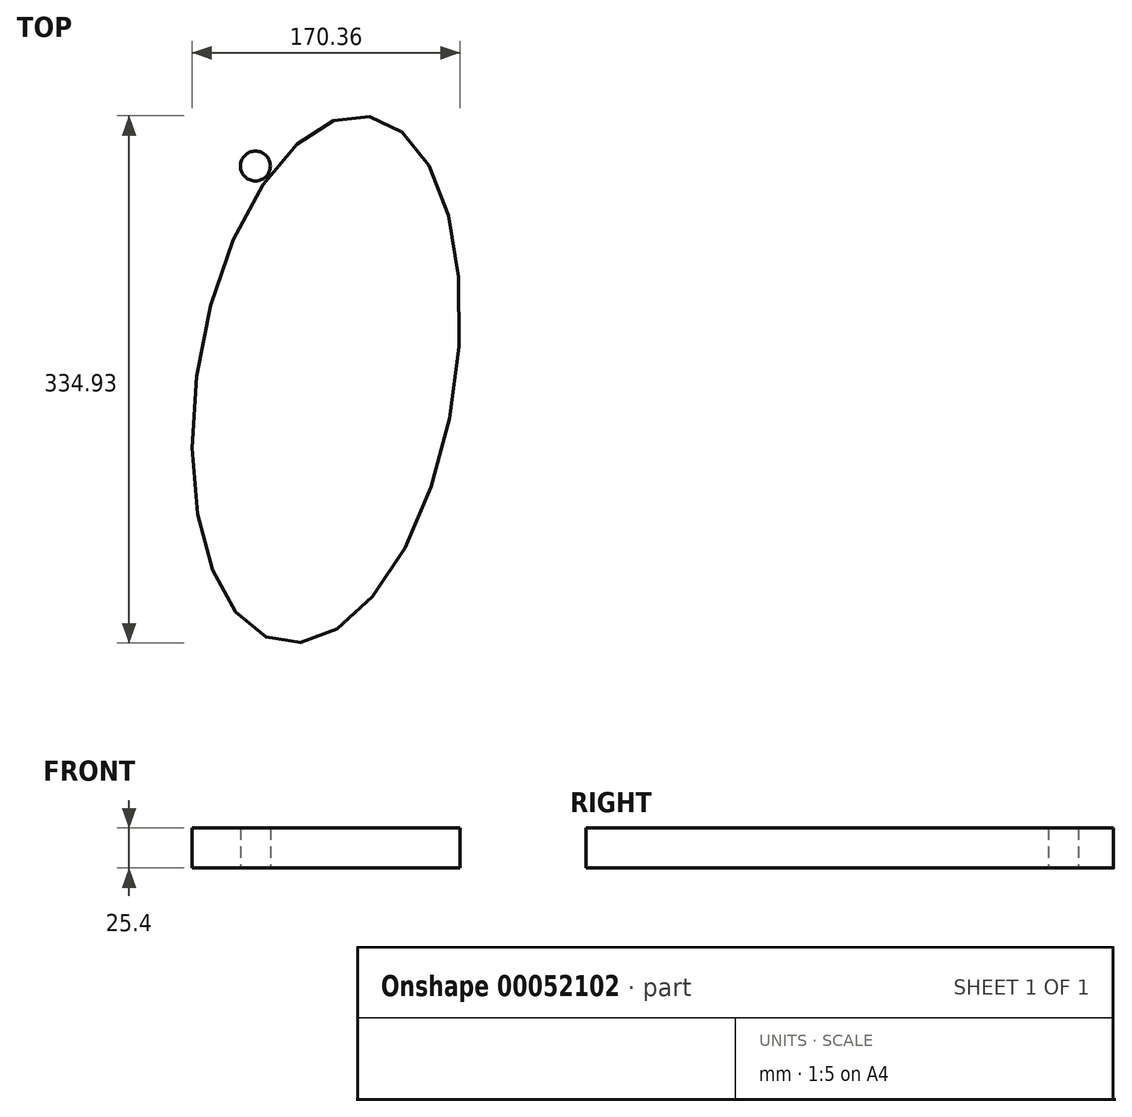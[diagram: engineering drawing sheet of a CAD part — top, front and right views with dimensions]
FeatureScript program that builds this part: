
annotation { "Feature Type Name" : "Feature", "Feature Type Description" : "" }
export const myFeature = defineFeature(function(context is Context, id is Id, definition is map)
    precondition{}
    {
        {
            var Q0;
            Q0=qCreatedBy(makeId("Top.planeOp"),FACE);
            var sketch = newSketch(context, id + "F0", { "sketchPlane" : qUnion([Q0])});
            skCircle(sketch, "E0", {"center": v(-20.86, 37.16) * mm, "radius": 9.48 * mm});
            skEllipse(sketch, "E1", {"center": v(24, -98.4) * mm, "majorRadius": 169.19 * mm, "minorRadius": 81.7 * mm, "majorAxis": v(0.16, 0.99)});
            skSolve(sketch);
        }
        {
            var Q0;
            Q0 = qSketchRegion(id + "F0", true);
            extrude(context, id + "F1", {"entities" : qUnion([Q0]), "endBound" : BoundingType.SYMMETRIC, "depth" : 25.4 * mm});
        }
    });
